# Revit family: Lighting-Industriale-GEWISS-ESALITE-HB-APPARECCHI-LED_16K_DALI
name_source: partatom
category: Apparecchi per illuminazione
units: mm (PartAtom-declared; Revit-internal decimal feet)

## family parameters
Condiviso = No
Host = Superficie
Punto di calcolo locali = Sì
Quota connettore circolare = Usa diametro
Sorgente d'illuminazione = No
Taglio con vuoti quando caricato = No
Tipo di parte = Normale

## types (1)
- Lighting-Industriale-GEWISS-ESALITE-HB-APPARECCHI-LED_16K_DALI
    Applicazione = Interno / Esterno
    Catalogo = LIGHTING
    Catalogo Serie = ESALITE HB - 16K
    Classe di efficienza LED integrati = A ÷ A++
    Classe isolamento = I
    Codice Electrocod = 2444
    Colore = Grigio RAL 9006
    Corrente di pilotaggio. = 0,599999999999999A
    Descrizione = ESALITE 16K ELL.5700K PLAF+V.GR.DALI
    Flusso nominale (lm) = 17000
    Garanzia = 5 anni
    Grado di protezione = IP66
    IDF = 601e2add-3ac0-41d0-ad3b-f966b47d6144
    IDT = a54f4c13e4cb438fafd2955485c5441c
    Immagine tipo = ESALITE_HB.jpg
    Lampada: = LED - Non sostituibile
    Life time L90B10 (Tq 25°C) = 100000H
    Life time L90B10 (Tq 50°C) = 50000H
    Lumen output (lm) = 13600
    Modello = GWS6335GD57K
    Ottica = Ellittica
    Peso (kg): = 7,5
    Potenza di sistema = 125W
    Potenza di sitema = Wxxx
    Produttore = GEWISS S.p.A.
    Prospetto di default = 1219 mm
    Resistenza agli urti = IK08
    Resistenza alle sovratensioni : = 8KV in modalità comune; 6KV in modalità differenziale
    SEO = High bay
    Scheda Tecnica = https://www.gewiss.com
    Schermo = Vetro temprato
    Temperatura di colore: = 5700 K (CRI>80)
    Temperatura di utilizzo = -30 +50 °C
    Tensione = 220/240 V - 50/60 Hz
    Tipo alimentatore = Driver Led Dali
    URL = https://www.gewiss.com
    Versione file RFA = 20.11
    Versioni = Luce fredda 5700K
